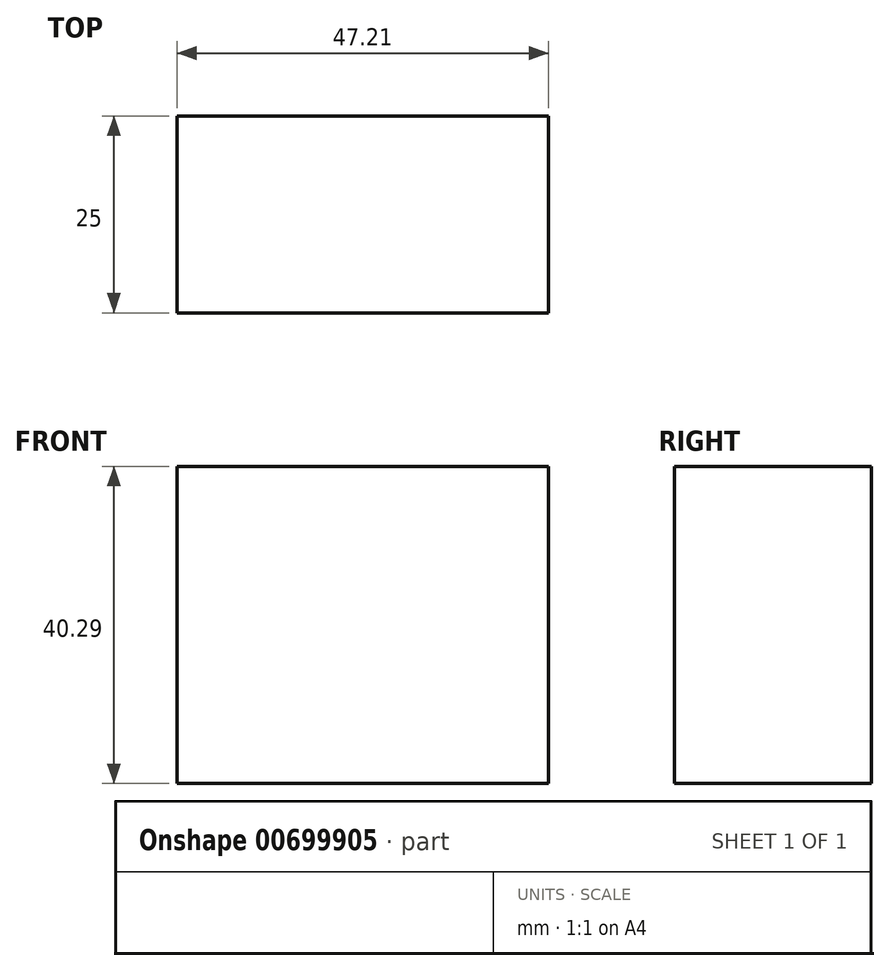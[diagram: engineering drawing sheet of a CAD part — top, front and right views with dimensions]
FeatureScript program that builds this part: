
annotation { "Feature Type Name" : "Feature", "Feature Type Description" : "" }
export const myFeature = defineFeature(function(context is Context, id is Id, definition is map)
    precondition{}
    {
        {
            var Q0;
            Q0=qCreatedBy(makeId("Front.planeOp"),FACE);
            var sketch = newSketch(context, id + "F0", { "sketchPlane" : qUnion([Q0])});
            skLineSegment(sketch, "E0.bottom", {"start": v(-23.11, 23.53) * mm, "end": v(24.1, 23.53) * mm});
            skLineSegment(sketch, "E0.top", {"start": v(-23.11, -16.76) * mm, "end": v(24.1, -16.76) * mm});
            skLineSegment(sketch, "E0.left", {"start": v(-23.11, 23.53) * mm, "end": v(-23.11, -16.76) * mm});
            skLineSegment(sketch, "E0.right", {"start": v(24.1, 23.53) * mm, "end": v(24.1, -16.76) * mm});
            skSolve(sketch);
        }
        {
            var Q0;
            Q0 = qSketchRegion(id + "F0", true);
            extrude(context, id + "F1", {"entities" : qUnion([Q0]), "depth" : 25 * mm, "offsetDistance" : 25 * mm});
        }
    });
